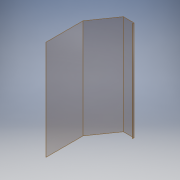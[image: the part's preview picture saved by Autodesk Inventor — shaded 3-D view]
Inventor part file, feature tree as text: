
AUTODESK INVENTOR PART (.ipt)
format: ipt  version: 2018 (Build 220112000, 112)  size: 108,032 bytes
history: native  units: mm
features: extrude x1, sketch x1
ambient origin geometry x8: Origin, YZ Plane, XZ Plane, XY Plane, X Axis, Y Axis, Z Axis, Center Point
bodies: Solid1 (feature_tree)
feature tree (2):
  extrude  "Extrusion1"  Depth=130.0mm
  sketch  "Sketch1"  dims[d0=20.0mm d1=130.0mm d2=21.816616mm d3=350.0mm d4=448.421mm d5=4.0mm d6=1200.0mm d7=0.0mm]
